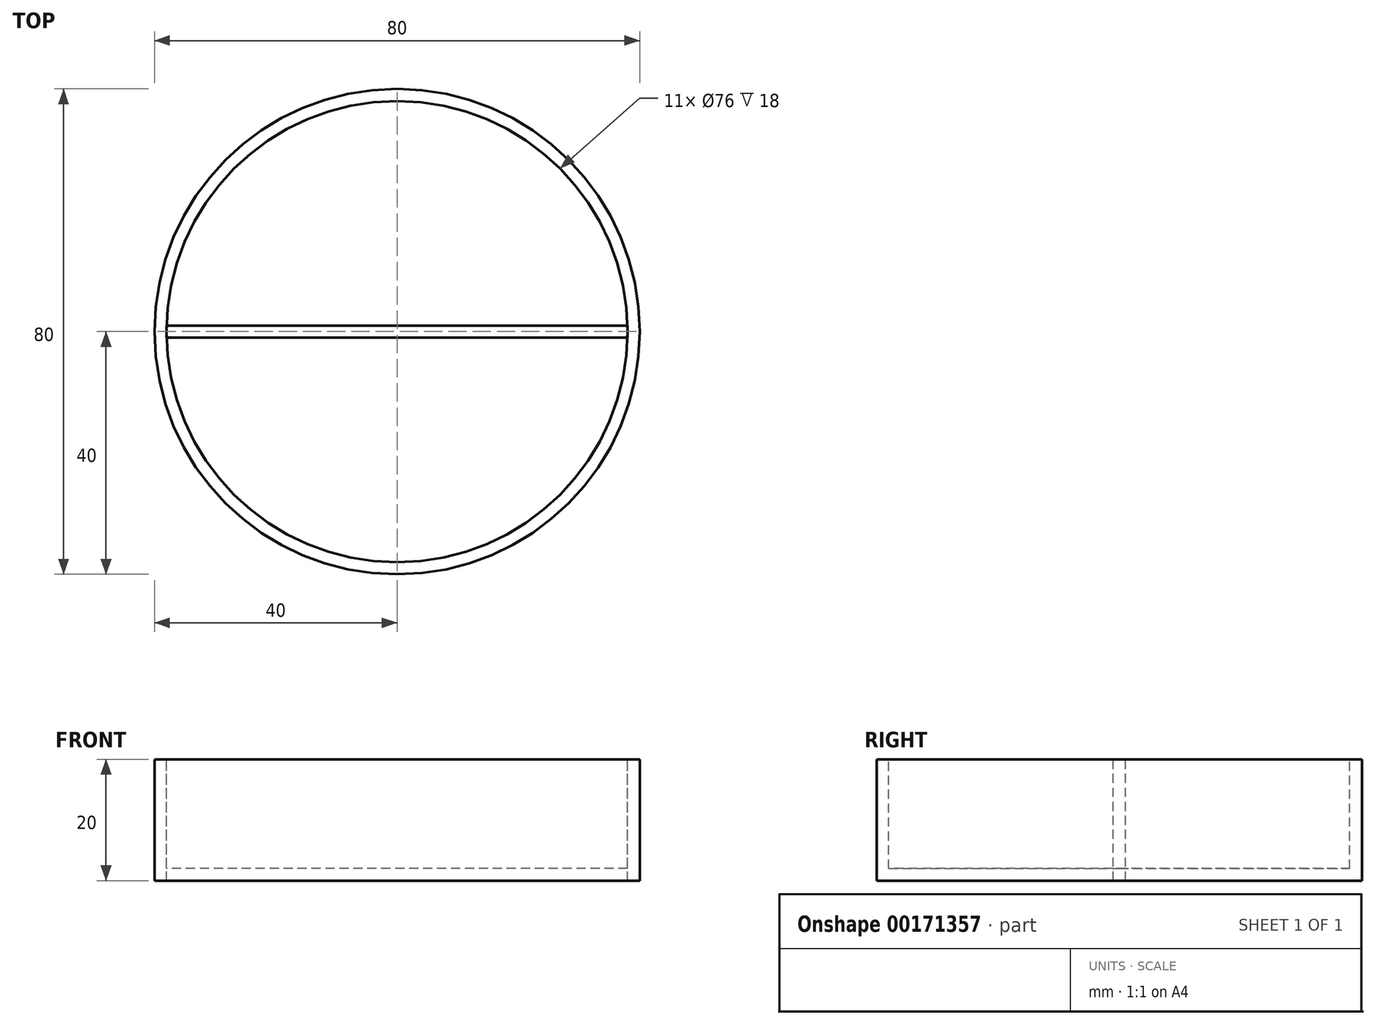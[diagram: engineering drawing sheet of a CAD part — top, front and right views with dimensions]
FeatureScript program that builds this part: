
annotation { "Feature Type Name" : "Feature", "Feature Type Description" : "" }
export const myFeature = defineFeature(function(context is Context, id is Id, definition is map)
    precondition{}
    {
        {
            var Q0;
            Q0=qCreatedBy(makeId("Top.planeOp"),FACE);
            var sketch = newSketch(context, id + "F0", { "sketchPlane" : qUnion([Q0])});
            skCircle(sketch, "E0", {"center": v(0, 0) * mm, "radius": 40 * mm});
            skSolve(sketch);
        }
        {
            var Q0;
            Q0=makeQuery(id+"F0.imprint","IMPRINT",FACE,{"disambiguationData":[TD([[makeQuery(id+"F0.imprint","IMPRINT",EDGE,{"derivedFrom":sQuery(id+"F0.wireOp",EDGE,"E0")}),1.0]])]});
            extrude(context, id + "F1", {"entities" : qUnion([Q0]), "depth" : 20 * mm});
        }
        {
            var Q0;
            Q0=makeQuery(id+"F1.opExtrude","CAP_FACE",FACE,{"disambiguationData":[OSD([sQuery(id+"F0.wireOp",EDGE,"E0")])],"isStart":false});
            var sketch = newSketch(context, id + "F2", { "sketchPlane" : qUnion([Q0])});
            skCircle(sketch, "E1", {"center": v(0, 0) * mm, "radius": 38 * mm});
            skSolve(sketch);
        }
        {
            var Q0;
            Q0=makeQuery(id+"F2.imprint","IMPRINT",FACE,{"disambiguationData":[TD([[makeQuery(id+"F2.imprint","IMPRINT",EDGE,{"derivedFrom":sQuery(id+"F2.wireOp",EDGE,"E1")}),1.0]])]});
            extrude(context, id + "F3", {"entities" : qUnion([Q0]), "operationType" : NewBodyOperationType.REMOVE, "oppositeDirection" : true, "depth" : 18 * mm});
        }
        {
            var Q0;
            Q0=makeQuery(id+"F1.opExtrude","CAP_FACE",FACE,{"disambiguationData":[OSD([sQuery(id+"F0.wireOp",EDGE,"E0")])],"isStart":false});
            var sketch = newSketch(context, id + "F4", { "sketchPlane" : qUnion([Q0])});
            skLineSegment(sketch, "E2", {"start": v(-38, 0) * mm, "end": v(-38, 1) * mm});
            skLineSegment(sketch, "E3.bottom", {"start": v(-38, 1) * mm, "end": v(37.99, 1) * mm});
            skLineSegment(sketch, "E3.top", {"start": v(-38, -1) * mm, "end": v(37.99, -1) * mm});
            skLineSegment(sketch, "E3.left", {"start": v(-38, 1) * mm, "end": v(-38, -1) * mm});
            skLineSegment(sketch, "E3.right", {"start": v(37.99, 1) * mm, "end": v(37.99, -1) * mm});
            skLineSegment(sketch, "E4", {"start": v(0, 1) * mm, "end": v(-1, 1) * mm, "construction": true});
            skLineSegment(sketch, "E5.bottom", {"start": v(-1, 1) * mm, "end": v(1, 1) * mm});
            skLineSegment(sketch, "E5.top", {"start": v(-1, 37.99) * mm, "end": v(1, 37.99) * mm});
            skLineSegment(sketch, "E5.left", {"start": v(-1, 1) * mm, "end": v(-1, 37.99) * mm});
            skLineSegment(sketch, "E5.right", {"start": v(1, 1) * mm, "end": v(1, 37.99) * mm});
            skSolve(sketch);
        }
        {
            var Q0;
            {var subQ2=sQuery(id+"F4.wireOp",EDGE,"E5.bottom");Q0=makeQuery(id+"F4.imprint","IMPRINT",FACE,{"disambiguationData":[TD([[makeQuery(id+"F4.imprint","IMPRINT",EDGE,{"derivedFrom":subQ2}),1.0]])]});}
            var Q1;
            {var subQ0=sQuery(id+"F4.wireOp",EDGE,"E3.right");Q1=makeQuery(id+"F4.imprint","IMPRINT",FACE,{"disambiguationData":[TD([[makeQuery(id+"F4.imprint","IMPRINT",EDGE,{"derivedFrom":subQ0}),-1.0]])]});}
            extrude(context, id + "F5", {"entities" : qUnion([Q0, Q1]), "oppositeDirection" : true, "depth" : 20 * mm});
        }
    });
